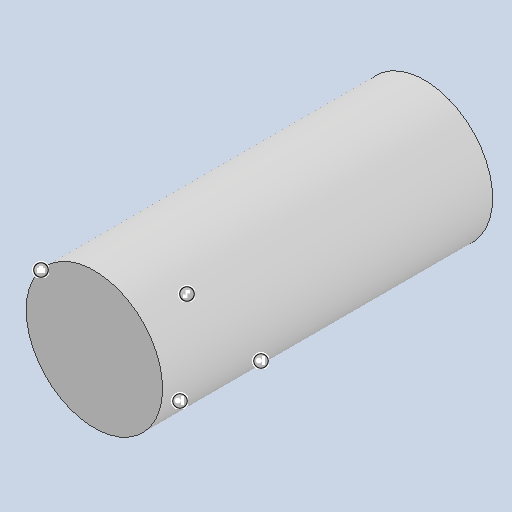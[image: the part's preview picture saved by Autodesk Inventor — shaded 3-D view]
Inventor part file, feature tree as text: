
AUTODESK INVENTOR PART (.ipt)
format: ipt  version: 2023.2 (Build 272271000, 271)  size: 100,352 bytes
history: native  units: mm
features: extrude x1, sketch x1
ambient origin geometry x8: Origin, YZ Plane, XZ Plane, XY Plane, X Axis, Y Axis, Z Axis, Center Point
bodies: Solid1 (feature_tree)
feature tree (2):
  extrude  "Extrusion1"  TaperAngle=0.0deg  [1 undecoded]
  sketch  "Sketch1"  dims[d2=0.0mm d3=0.0mm d4=0.0mm d9=0.0mm d10=0.0mm]
note: 1 required parameter value undecoded (feature->parameter linkage not recoverable at this tier; creation-order binding heuristic only, values carry confidence <= 0.55)
